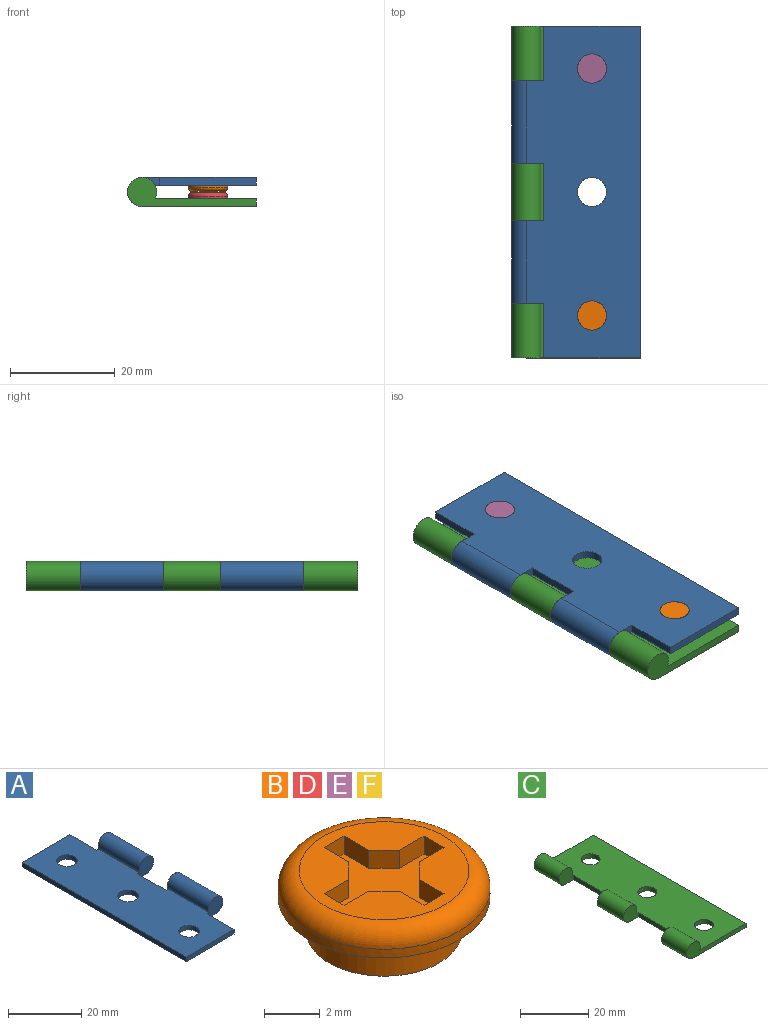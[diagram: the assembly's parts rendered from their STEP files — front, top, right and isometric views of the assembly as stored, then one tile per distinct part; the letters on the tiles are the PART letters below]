
ASSEMBLY  parts=6 mates=5
PART A: 17 faces, bbox 24.6x63.5x5.6 mm
  f0: plane 63.5x19.36mm, normal (0,0,1), area 1129.7mm2, adj f1,f2,f3,f4,f5,f6,f7,f8
  f1: plane 10.41x1.52mm, normal (1,0,0), area 15.9mm2, adj f0,f2,f13,f14
  f2: plane 6.1x5.59mm, normal (0,-1,0), area 26.8mm2, adj f0,f1,f14,f15
  f3: plane 6.1x5.59mm, normal (0,1,0), area 26.8mm2, adj f0,f4,f14,f15
  f4: plane 10.92x1.52mm, normal (1,0,0), area 16.6mm2, adj f0,f3,f5,f14
  f5: plane 6.1x5.59mm, normal (0,-1,0), area 26.8mm2, adj f0,f4,f14,f16
  f6: plane 6.1x5.59mm, normal (0,1,0), area 26.8mm2, adj f0,f7,f14,f16
  f7: plane 10.41x1.52mm, normal (1,0,0), area 15.9mm2, adj f0,f6,f8,f14
  f8: plane 18.54x1.52mm, normal (0,1,0), area 28.3mm2, adj f0,f7,f9,f14
  f9: plane 63.5x1.52mm, normal (-1,0,0), area 96.8mm2, adj f0,f8,f13,f14
  f10: cylinder r=2.79mm len=5.59mm, axis (0,0,-1), area 26.8mm2, adj f0,f14
  f11: cylinder r=2.79mm len=5.59mm, axis (0,0,-1), area 26.8mm2, adj f0,f14
  f12: cylinder r=2.79mm len=5.59mm, axis (0,0,-1), area 26.8mm2, adj f0,f14
  f13: plane 18.54x1.52mm, normal (0,-1,0), area 28.3mm2, adj f0,f1,f9,f14
  f14: plane 63.5x21.84mm, normal (0,0,-1), area 1208.7mm2, adj f1,f2,f3,f4,f5,f6,f7,f8
  f15: cylinder r=2.79mm len=15.88mm, axis (0,1,0), area 229.9mm2, adj f0,f2,f3,f14
  f16: cylinder r=2.79mm len=15.88mm, axis (0,-1,0), area 229.9mm2, adj f0,f5,f6,f14
PART B: 23 faces, bbox 8.2x8.2x2.7 mm
  f0: plane 6.1x6.1mm, normal (0,0,1), area 18.7mm2, adj f5,f6,f7,f8,f9,f10,f11,f12
  f1: plane 5.59x5.59mm, normal (0,0,-1), area 24.5mm2, adj f2
  f2: cylinder r=2.79mm len=5.59mm, axis (0,0,1), area 26.8mm2, adj f1,f3
  f3: plane 7.62x7.62mm, normal (0,0,-1), area 21.1mm2, adj f2,f4
  f4: cylinder r=3.81mm len=7.62mm, axis (0,0,1), area 9.1mm2, adj f3,f22
  f5: plane 1.25x0.79mm, normal (1,0,0), area 1mm2, adj f0,f6,f20,f21
  f6: plane 1.02x0.79mm, normal (0,1,0), area 0.8mm2, adj f0,f5,f7,f21
  f7: plane 1.25x0.79mm, normal (-1,0,0), area 1mm2, adj f0,f6,f8,f21
  f8: plane 0.79x0.78mm, normal (-0.71,0.71,0), area 0.9mm2, adj f0,f7,f9,f21
  f9: plane 1.25x0.79mm, normal (0,1,0), area 1mm2, adj f0,f8,f10,f21
  f10: plane 1.02x0.79mm, normal (-1,0,0), area 0.8mm2, adj f0,f9,f11,f21
  f11: plane 1.25x0.79mm, normal (0,-1,0), area 1mm2, adj f0,f10,f12,f21
  f12: plane 0.79x0.78mm, normal (-0.71,-0.71,0), area 0.9mm2, adj f0,f11,f13,f21
  f13: plane 1.25x0.79mm, normal (-1,0,0), area 1mm2, adj f0,f12,f14,f21
  f14: plane 1.02x0.79mm, normal (0,-1,0), area 0.8mm2, adj f0,f13,f15,f21
  f15: plane 1.25x0.79mm, normal (1,0,0), area 1mm2, adj f0,f14,f16,f21
  f16: plane 0.79x0.78mm, normal (0.71,-0.71,0), area 0.9mm2, adj f0,f15,f17,f21
  f17: plane 1.25x0.79mm, normal (0,-1,0), area 1mm2, adj f0,f16,f18,f21
  f18: plane 1.02x0.79mm, normal (1,0,0), area 0.8mm2, adj f0,f17,f19,f21
  f19: plane 1.25x0.79mm, normal (0,1,0), area 1mm2, adj f0,f18,f20,f21
  f20: plane 0.79x0.78mm, normal (0.71,0.71,0), area 0.9mm2, adj f0,f5,f19,f21
  f21: plane 5.08x5.08mm, normal (0,0,1), area 10.5mm2, adj f5,f6,f7,f8,f9,f10,f11,f12
  f22: torus R=3.05mm, axis (0,0,-1), area 26.6mm2, adj f0,f4
PART C: 17 faces, bbox 24.6x63.5x5.6 mm
  f0: plane 63.5x19.36mm, normal (0,0,1), area 1129.7mm2, adj f1,f2,f3,f4,f5,f6,f7,f8
  f1: plane 24.64x5.59mm, normal (0,-1,0), area 55.1mm2, adj f0,f2,f13,f15
  f2: plane 63.5x1.52mm, normal (1,0,0), area 96.8mm2, adj f0,f1,f3,f13
  f3: plane 24.64x5.59mm, normal (0,1,0), area 55.1mm2, adj f0,f2,f13,f16
  f4: plane 6.1x5.59mm, normal (0,-1,0), area 26.8mm2, adj f0,f5,f13,f16
  f5: plane 15.88x1.52mm, normal (-1,0,0), area 24.2mm2, adj f0,f4,f6,f13
  f6: plane 6.1x5.59mm, normal (0,1,0), area 26.8mm2, adj f0,f5,f13,f14
  f7: plane 6.1x5.59mm, normal (0,-1,0), area 26.8mm2, adj f0,f8,f13,f14
  f8: plane 15.88x1.52mm, normal (-1,0,0), area 24.2mm2, adj f0,f7,f9,f13
  f9: plane 6.1x5.59mm, normal (0,1,0), area 26.8mm2, adj f0,f8,f13,f15
  f10: cylinder r=2.79mm len=5.59mm, axis (0,0,-1), area 26.8mm2, adj f0,f13
  f11: cylinder r=2.79mm len=5.59mm, axis (0,0,-1), area 26.8mm2, adj f0,f13
  f12: cylinder r=2.79mm len=5.59mm, axis (0,0,-1), area 26.8mm2, adj f0,f13
  f13: plane 63.5x21.84mm, normal (0,0,-1), area 1208.7mm2, adj f1,f2,f3,f4,f5,f6,f7,f8
  f14: cylinder r=2.79mm len=10.92mm, axis (0,-1,0), area 158.2mm2, adj f0,f6,f7,f13
  f15: cylinder r=2.79mm len=10.41mm, axis (0,-1,0), area 150.8mm2, adj f0,f1,f9,f13
  f16: cylinder r=2.79mm len=10.41mm, axis (0,1,0), area 150.8mm2, adj f0,f3,f4,f13
PART D: same geometry as B
PART E: same geometry as B
PART F: same geometry as B
PLACE A rot(axis=(0,1,0),180deg) t=(-3.3,0,0)mm
PLACE B rot(axis=(1,0,0),180deg) t=(9.27,-23.62,0)mm
PLACE C rot(axis=(-0.01,1,0.04),0deg) t=(-3.3,0,-5.59)mm
PLACE D rot(axis=(0,0,1),90deg) t=(9.27,-23.62,-5.59)mm
PLACE E rot(axis=(1,0,0),180deg) t=(9.27,23.62,0)mm
PLACE F rot(axis=(-0.01,1,0.04),0deg) t=(9.27,23.62,-5.59)mm
MATE fastened B.f2 <-> A.f12  axis (0,0,1) through (9.27,-23.62,0)mm
MATE fastened D.f2 <-> C.f10  axis (0,0,-1) through (9.27,-23.62,-5.59)mm
MATE revolute C.f14 <-> A.f15  axis (0,1,0) through (-3.3,-21.34,-2.79)mm
MATE fastened C.f12 <-> F.f2  axis (0,0,-1) through (9.27,23.62,-5.59)mm
MATE fastened A.f11 <-> E.f2  axis (0,0,1) through (9.27,23.62,0)mm
